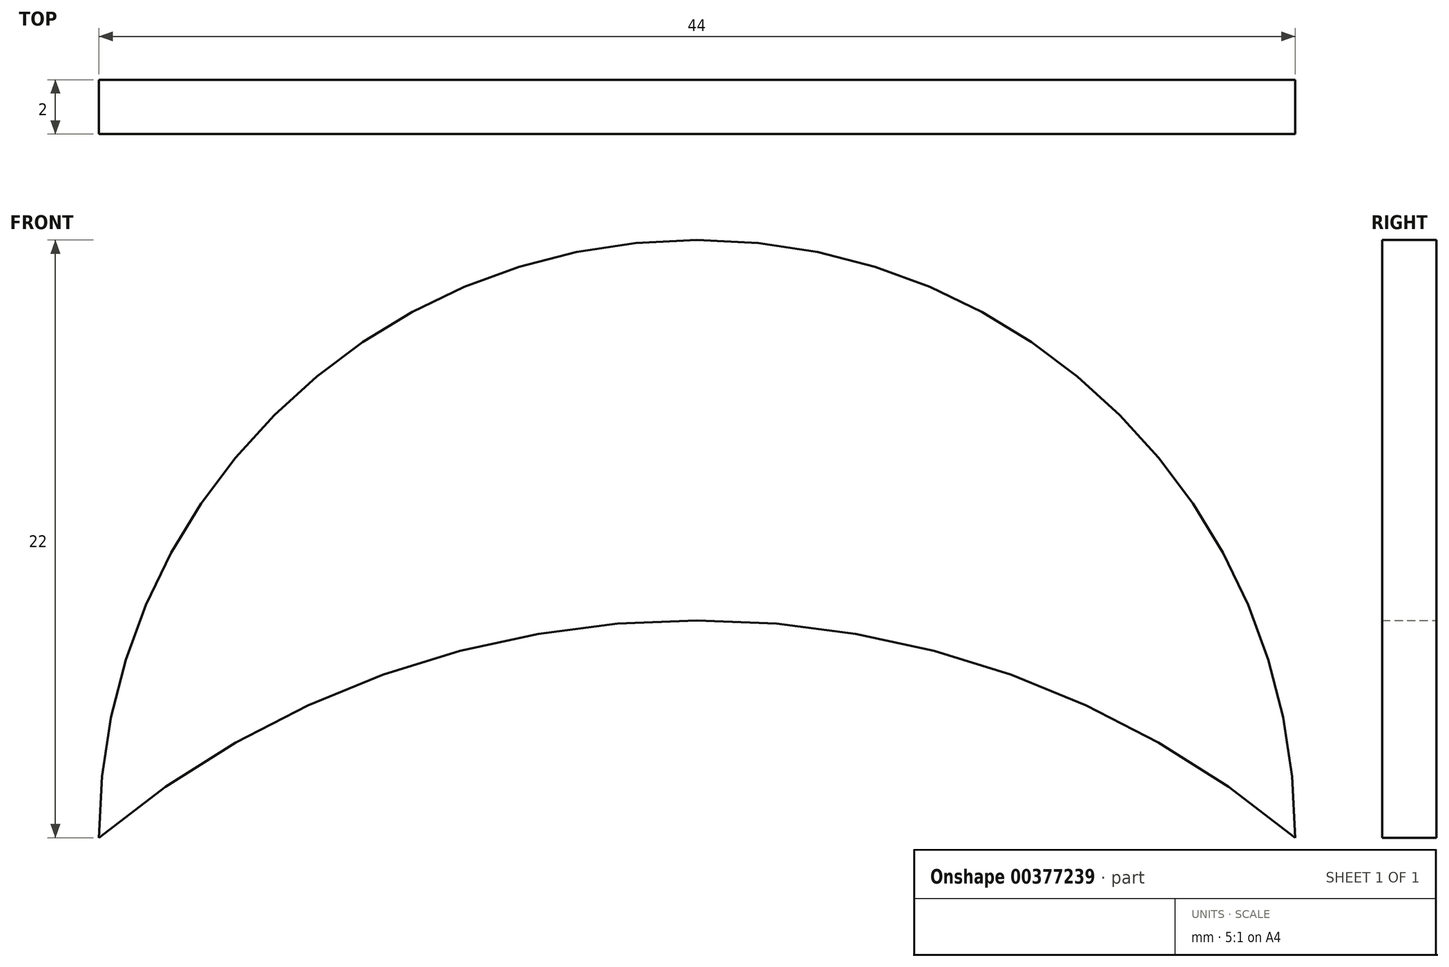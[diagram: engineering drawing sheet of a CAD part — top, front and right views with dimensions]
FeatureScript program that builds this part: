
annotation { "Feature Type Name" : "Feature", "Feature Type Description" : "" }
export const myFeature = defineFeature(function(context is Context, id is Id, definition is map)
    precondition{}
    {
        {
            var Q0;
            Q0=qCreatedBy(makeId("Front.planeOp"),FACE);
            var sketch = newSketch(context, id + "F0", { "sketchPlane" : qUnion([Q0])});
            skArc(sketch, "E0", {"start": v(22, 0) * mm, "mid": v(0, 22) * mm, "end": v(-22, 0) * mm});
            skArc(sketch, "E1", {"start": v(22, 0) * mm, "mid": v(0, 8) * mm, "end": v(-22, 0) * mm});
            skSolve(sketch);
        }
        {
            var Q0;
            Q0=makeQuery(id+"F0.imprint","IMPRINT",FACE,{"disambiguationData":[TD([[makeQuery(id+"F0.imprint","IMPRINT",EDGE,{"derivedFrom":sQuery(id+"F0.wireOp",EDGE,"E0")}),1.0]])]});
            extrude(context, id + "F1", {"entities" : qUnion([Q0]), "depth" : 2 * mm});
        }
    });
